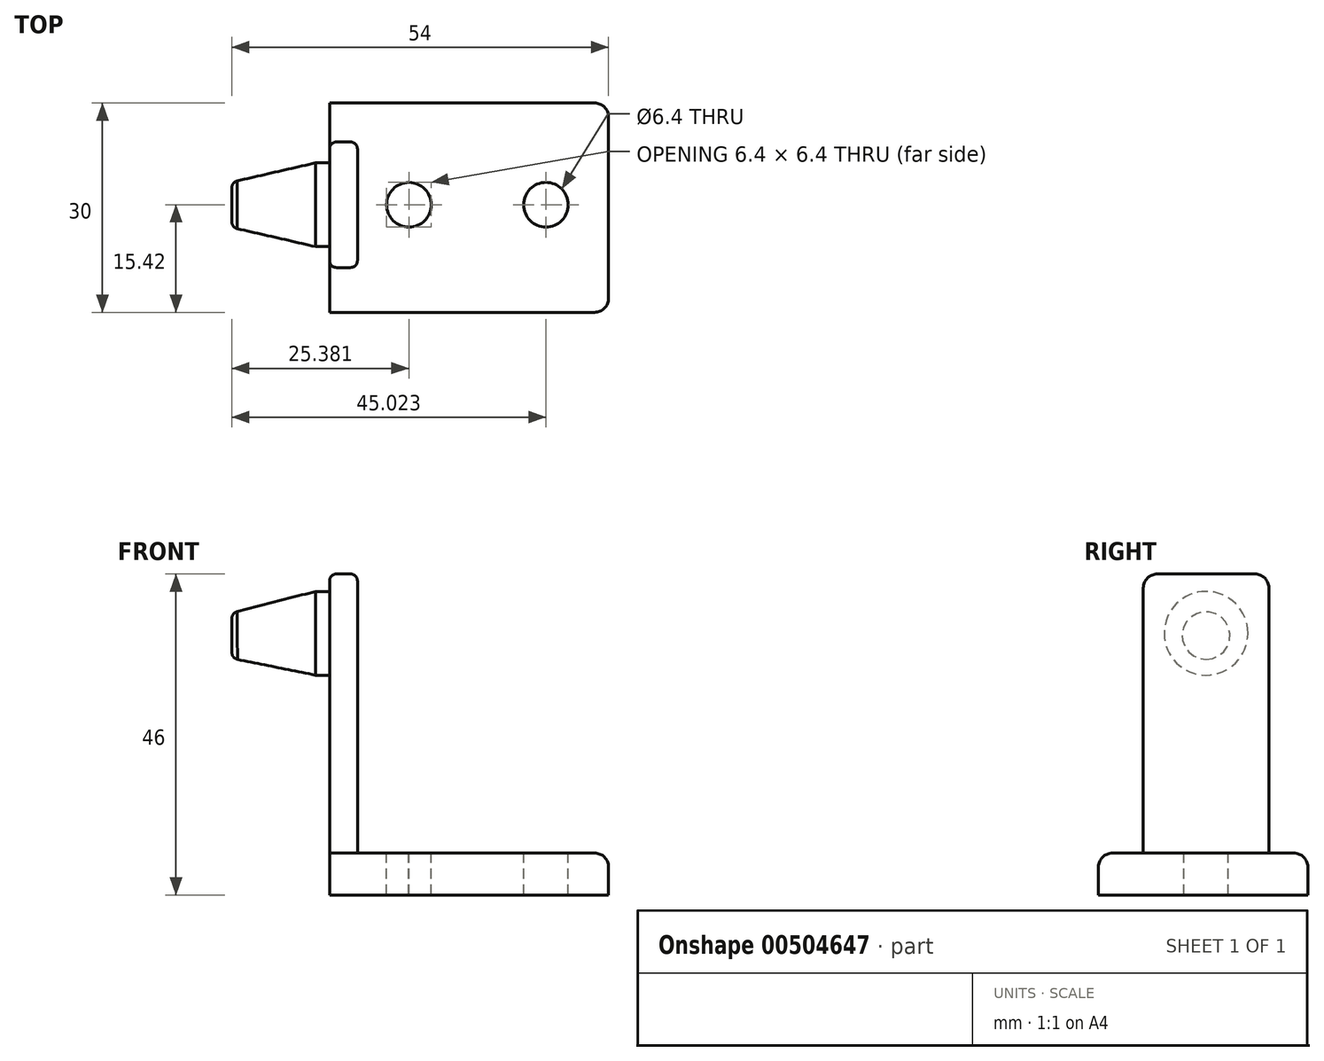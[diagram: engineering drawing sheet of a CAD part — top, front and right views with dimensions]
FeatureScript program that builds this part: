
annotation { "Feature Type Name" : "Feature", "Feature Type Description" : "" }
export const myFeature = defineFeature(function(context is Context, id is Id, definition is map)
    precondition{}
    {
        {
            var Q0;
            Q0=qCreatedBy(makeId("Top.planeOp"),FACE);
            var sketch = newSketch(context, id + "F0", { "sketchPlane" : qUnion([Q0])});
            skLineSegment(sketch, "E0.bottom", {"start": v(0, 14.58) * mm, "end": v(40, 14.58) * mm});
            skLineSegment(sketch, "E0.top", {"start": v(0, -15.42) * mm, "end": v(40, -15.42) * mm});
            skLineSegment(sketch, "E0.left", {"start": v(0, 14.58) * mm, "end": v(0, -15.42) * mm});
            skLineSegment(sketch, "E0.right", {"start": v(40, 14.58) * mm, "end": v(40, -15.42) * mm});
            skSolve(sketch);
        }
        {
            var Q0;
            Q0=qSketchRegion(id+"F0",true);
            extrude(context, id + "F1", {"entities" : qUnion([Q0]), "depth" : 6 * mm});
        }
        {
            var Q0;
            Q0=makeQuery(id+"F1.opExtrude","CAP_FACE",FACE,{"disambiguationData":[OSD([sQuery(id+"F0.wireOp",EDGE,"E0.bottom"),sQuery(id+"F0.wireOp",EDGE,"E0.top"),sQuery(id+"F0.wireOp",EDGE,"E0.left"),sQuery(id+"F0.wireOp",EDGE,"E0.right")])],"isStart":false});
            var sketch = newSketch(context, id + "F2", { "sketchPlane" : qUnion([Q0])});
            skLineSegment(sketch, "E1.bottom", {"start": v(0, 9) * mm, "end": v(4, 9) * mm});
            skLineSegment(sketch, "E1.top", {"start": v(0, -9) * mm, "end": v(4, -9) * mm});
            skLineSegment(sketch, "E1.left", {"start": v(0, 9) * mm, "end": v(0, -9) * mm});
            skLineSegment(sketch, "E1.right", {"start": v(4, 9) * mm, "end": v(4, -9) * mm});
            skSolve(sketch);
        }
        {
            var Q0;
            Q0=makeQuery(id+"F2.imprint","IMPRINT",FACE,{"disambiguationData":[TD([[makeQuery(id+"F2.imprint","IMPRINT",EDGE,{"derivedFrom":sQuery(id+"F2.wireOp",EDGE,"E1.bottom")}),-1.0]])]});
            extrude(context, id + "F3", {"entities" : qUnion([Q0]), "operationType" : NewBodyOperationType.ADD, "depth" : 40 * mm});
        }
        {
            var Q0;
            Q0=makeQuery(id+"F3.opExtrude","SWEPT_FACE",FACE,{"disambiguationData":[OSD([sQuery(id+"F2.wireOp",EDGE,"E1.right")])]});
            var sketch = newSketch(context, id + "F4", { "sketchPlane" : qUnion([Q0])});
            skLineSegment(sketch, "E2", {"start": v(0, 46) * mm, "end": v(0, 6) * mm, "construction": true});
            skLineSegment(sketch, "E3", {"start": v(-9, 37.5) * mm, "end": v(9, 37.5) * mm});
            skCircle(sketch, "E4", {"center": v(0, 37.5) * mm, "radius": 6 * mm});
            skSolve(sketch);
        }
        {
            var Q0;
            Q0=qSketchRegion(id+"F4",true);
            extrude(context, id + "F5", {"entities" : qUnion([Q0]), "operationType" : NewBodyOperationType.ADD, "oppositeDirection" : true, "depth" : 6 * mm});
        }
        {
            var Q0;
            Q0=makeQuery(id+"F5.opExtrude","CAP_FACE",FACE,{"disambiguationData":[OSD([sQuery(id+"F4.wireOp",EDGE,"E4")])],"isStart":false});
            cPlane(context, id + "F6", {"entities" : qUnion([Q0]), "cplaneType" : CPlaneType.OFFSET, "offset" : 12 * mm, "width" : 150 * mm, "height" : 150 * mm});
        }
        {
            var Q0;
            Q0=qCreatedBy(id+"F6.planeOp",FACE);
            var sketch = newSketch(context, id + "F7", { "sketchPlane" : qUnion([Q0])});
            skLineSegment(sketch, "E5", {"start": v(0, 37.17) * mm, "end": v(0, 37.17) * mm});
            skLineSegment(sketch, "E6", {"start": v(0, 37.17) * mm, "end": v(-8.55, 37.17) * mm, "construction": true});
            skCircle(sketch, "E7", {"center": v(0, 37.17) * mm, "radius": 3.25 * mm});
            skSolve(sketch);
        }
        {
            var Q0;
            Q0=makeQuery(id+"F1.opExtrude","CAP_FACE",FACE,{"disambiguationData":[OSD([sQuery(id+"F0.wireOp",EDGE,"E0.bottom"),sQuery(id+"F0.wireOp",EDGE,"E0.top"),sQuery(id+"F0.wireOp",EDGE,"E0.left"),sQuery(id+"F0.wireOp",EDGE,"E0.right")])],"isStart":false});
            var sketch = newSketch(context, id + "F8", { "sketchPlane" : qUnion([Q0])});
            skCircle(sketch, "E8", {"center": v(11.38, 0) * mm, "radius": 3.2 * mm});
            skCircle(sketch, "E9", {"center": v(31.02, 0) * mm, "radius": 3.2 * mm});
            skLineSegment(sketch, "E10", {"start": v(11.34, 3.2) * mm, "end": v(31.02, 3.2) * mm});
            skLineSegment(sketch, "E11", {"start": v(11.67, -3.19) * mm, "end": v(31.02, -3.2) * mm});
            skSolve(sketch);
        }
        {
            var Q0;
            {var subQ0=sQuery(id+"F8.wireOp",EDGE,"E9");var subQ1=makeQuery(id+"F8.imprint","INTERSECT",VERTEX,{"derivedFrom":[subQ0,sQuery(id+"F8.wireOp",EDGE,"E10")]});Q0=makeQuery(id+"F8.imprint","IMPRINT",FACE,{"disambiguationData":[TD([[makeQuery(id+"F8.imprint","IMPRINT",EDGE,{"disambiguationData":[TD([[subQ1,-1.0]])],"derivedFrom":subQ0}),1.0]])]});}
            var Q1;
            {var subQ0=sQuery(id+"F8.wireOp",EDGE,"E10");Q1=makeQuery(id+"F8.imprint","IMPRINT",FACE,{"disambiguationData":[TD([[makeQuery(id+"F8.imprint","IMPRINT",EDGE,{"derivedFrom":subQ0}),-1.0]])]});}
            var Q2;
            {var subQ0=sQuery(id+"F8.wireOp",EDGE,"E8");var subQ2=makeQuery(id+"F8.imprint","IMPRINT",VERTEX,{"derivedFrom":subQ0});Q2=makeQuery(id+"F8.imprint","IMPRINT",FACE,{"disambiguationData":[TD([[makeQuery(id+"F8.imprint","IMPRINT",EDGE,{"disambiguationData":[TD([[subQ2,1.0]])],"derivedFrom":subQ0}),1.0]])]});}
            extrude(context, id + "F9", {"entities" : qUnion([Q0, Q1, Q2]), "operationType" : NewBodyOperationType.REMOVE, "endBound" : BoundingType.THROUGH_ALL, "oppositeDirection" : true, "depth" : 25 * mm});
        }
        {
            var Q0;
            Q0=makeQuery(id+"F3.opExtrude","CAP_EDGE",EDGE,{"disambiguationData":[OSD([sQuery(id+"F2.wireOp",EDGE,"E1.right")])],"isStart":false});
            var Q1;
            Q1=makeQuery(id+"F3.opExtrude","SWEPT_EDGE",EDGE,{"disambiguationData":[OSD([sQuery(id+"F2.wireOp",EDGE,"E1.top"),sQuery(id+"F2.wireOp",EDGE,"E1.right")])]});
            var Q2;
            Q2=makeQuery(id+"F3.opExtrude","SWEPT_EDGE",EDGE,{"disambiguationData":[OSD([sQuery(id+"F2.wireOp",EDGE,"E1.bottom"),sQuery(id+"F2.wireOp",EDGE,"E1.right")])]});
            var Q3;
            Q3=makeQuery(id+"F3.opExtrude","CAP_EDGE",EDGE,{"disambiguationData":[OSD([sQuery(id+"F2.wireOp",EDGE,"E1.right")])],"isStart":true});
            var Q4;
            {var subQ0=sQuery(id+"F2.wireOp",EDGE,"E1.top");var subQ1=sQuery(id+"F0.wireOp",EDGE,"E0.left");var subQ2=sQuery(id+"F2.wireOp",EDGE,"E1.left");Q4=makeQuery(id+"F5.boolean.opBoolean","SPLIT",EDGE,{"disambiguationData":[TD([makeQuery(id+"F1.opExtrude","CAP_FACE",FACE,{"disambiguationData":[OSD([sQuery(id+"F0.wireOp",EDGE,"E0.bottom"),sQuery(id+"F0.wireOp",EDGE,"E0.top"),subQ1,sQuery(id+"F0.wireOp",EDGE,"E0.right")])],"isStart":false})])],"derivedFrom":makeQuery(id+"F3.opExtrude","SWEPT_EDGE",EDGE,{"disambiguationData":[OSD([subQ1,subQ0,subQ2])]})});}
            var Q5;
            {var subQ0=sQuery(id+"F2.wireOp",EDGE,"E1.bottom");var subQ1=sQuery(id+"F0.wireOp",EDGE,"E0.left");var subQ2=sQuery(id+"F2.wireOp",EDGE,"E1.left");Q5=makeQuery(id+"F5.boolean.opBoolean","SPLIT",EDGE,{"disambiguationData":[TD([makeQuery(id+"F1.opExtrude","CAP_FACE",FACE,{"disambiguationData":[OSD([sQuery(id+"F0.wireOp",EDGE,"E0.bottom"),sQuery(id+"F0.wireOp",EDGE,"E0.top"),subQ1,sQuery(id+"F0.wireOp",EDGE,"E0.right")])],"isStart":false})])],"derivedFrom":makeQuery(id+"F3.opExtrude","SWEPT_EDGE",EDGE,{"disambiguationData":[OSD([subQ1,subQ0,subQ2])]})});}
            var Q6;
            Q6=makeQuery(id+"F3.opExtrude","CAP_EDGE",EDGE,{"disambiguationData":[OSD([sQuery(id+"F2.wireOp",EDGE,"E1.left")])],"isStart":false});
            var Q7;
            Q7=makeQuery(id+"FxFCH0ypCKijwpu_1.opLoft","MID_CAP_EDGE",EDGE,{"disambiguationData":[OSD([sQuery(id+"F4.wireOp",EDGE,"E4"),sQuery(id+"F7.wireOp",EDGE,"FnkbBOsJ-T3qc-zvui-fy8C-9BorDEMkUiyw")])],"capPos":1.0});
            fillet(context, id + "F10", {"entities" : qUnion([Q0, Q1, Q2, Q3, Q4, Q5, Q6, Q7]), "radius" : 1 * mm, "tangentPropagation" : true, "allowEdgeOverflow" : false});
        }
        {
            var Q0;
            Q0=makeQuery(id+"F3.opExtrude","CAP_EDGE",EDGE,{"disambiguationData":[OSD([sQuery(id+"F2.wireOp",EDGE,"E1.bottom")])],"isStart":false});
            var Q1;
            Q1=makeQuery(id+"F3.opExtrude","CAP_EDGE",EDGE,{"disambiguationData":[OSD([sQuery(id+"F2.wireOp",EDGE,"E1.top")])],"isStart":false});
            var Q2;
            Q2=makeQuery(id+"F1.opExtrude","CAP_EDGE",EDGE,{"disambiguationData":[OSD([sQuery(id+"F0.wireOp",EDGE,"E0.top")])],"isStart":false});
            var Q3;
            Q3=makeQuery(id+"F1.opExtrude","CAP_EDGE",EDGE,{"disambiguationData":[OSD([sQuery(id+"F0.wireOp",EDGE,"E0.right")])],"isStart":false});
            var Q4;
            Q4=makeQuery(id+"F1.opExtrude","CAP_EDGE",EDGE,{"disambiguationData":[OSD([sQuery(id+"F0.wireOp",EDGE,"E0.bottom")])],"isStart":false});
            var Q5;
            Q5=makeQuery(id+"F1.opExtrude","SWEPT_EDGE",EDGE,{"disambiguationData":[OSD([sQuery(id+"F0.wireOp",EDGE,"E0.top"),sQuery(id+"F0.wireOp",EDGE,"E0.right")])]});
            var Q6;
            Q6=makeQuery(id+"F1.opExtrude","SWEPT_EDGE",EDGE,{"disambiguationData":[OSD([sQuery(id+"F0.wireOp",EDGE,"E0.bottom"),sQuery(id+"F0.wireOp",EDGE,"E0.right")])]});
            fillet(context, id + "F11", {"entities" : qUnion([Q0, Q1, Q2, Q3, Q4, Q5, Q6]), "radius" : 2 * mm, "tangentPropagation" : true, "allowEdgeOverflow" : false});
        }
        {
            var Q0;
            Q0=makeQuery(id+"F5.opExtrude","CAP_FACE",FACE,{"disambiguationData":[OSD([sQuery(id+"F4.wireOp",EDGE,"E4")])],"isStart":false});
            var Q1;
            Q1=makeQuery(id+"F7.imprint","IMPRINT",FACE,{"disambiguationData":[TD([[makeQuery(id+"F7.imprint","IMPRINT",EDGE,{"derivedFrom":sQuery(id+"F7.wireOp",EDGE,"E7")}),1.0]])]});
            loft(context, id + "F12", {"sheetProfilesArray" : [{ "sheetProfileEntities" : qUnion([Q0]) }, { "sheetProfileEntities" : qUnion([Q1]) }]});
        }
        {
            var Q0;
            Q0=makeQuery(id+"F12.opLoft","MID_CAP_EDGE",EDGE,{"disambiguationData":[OSD([sQuery(id+"F4.wireOp",EDGE,"E4"),sQuery(id+"F7.wireOp",EDGE,"E7")])],"capPos":1.0});
            fillet(context, id + "F13", {"entities" : qUnion([Q0]), "radius" : 1 * mm, "tangentPropagation" : true, "allowEdgeOverflow" : false});
        }
    });
